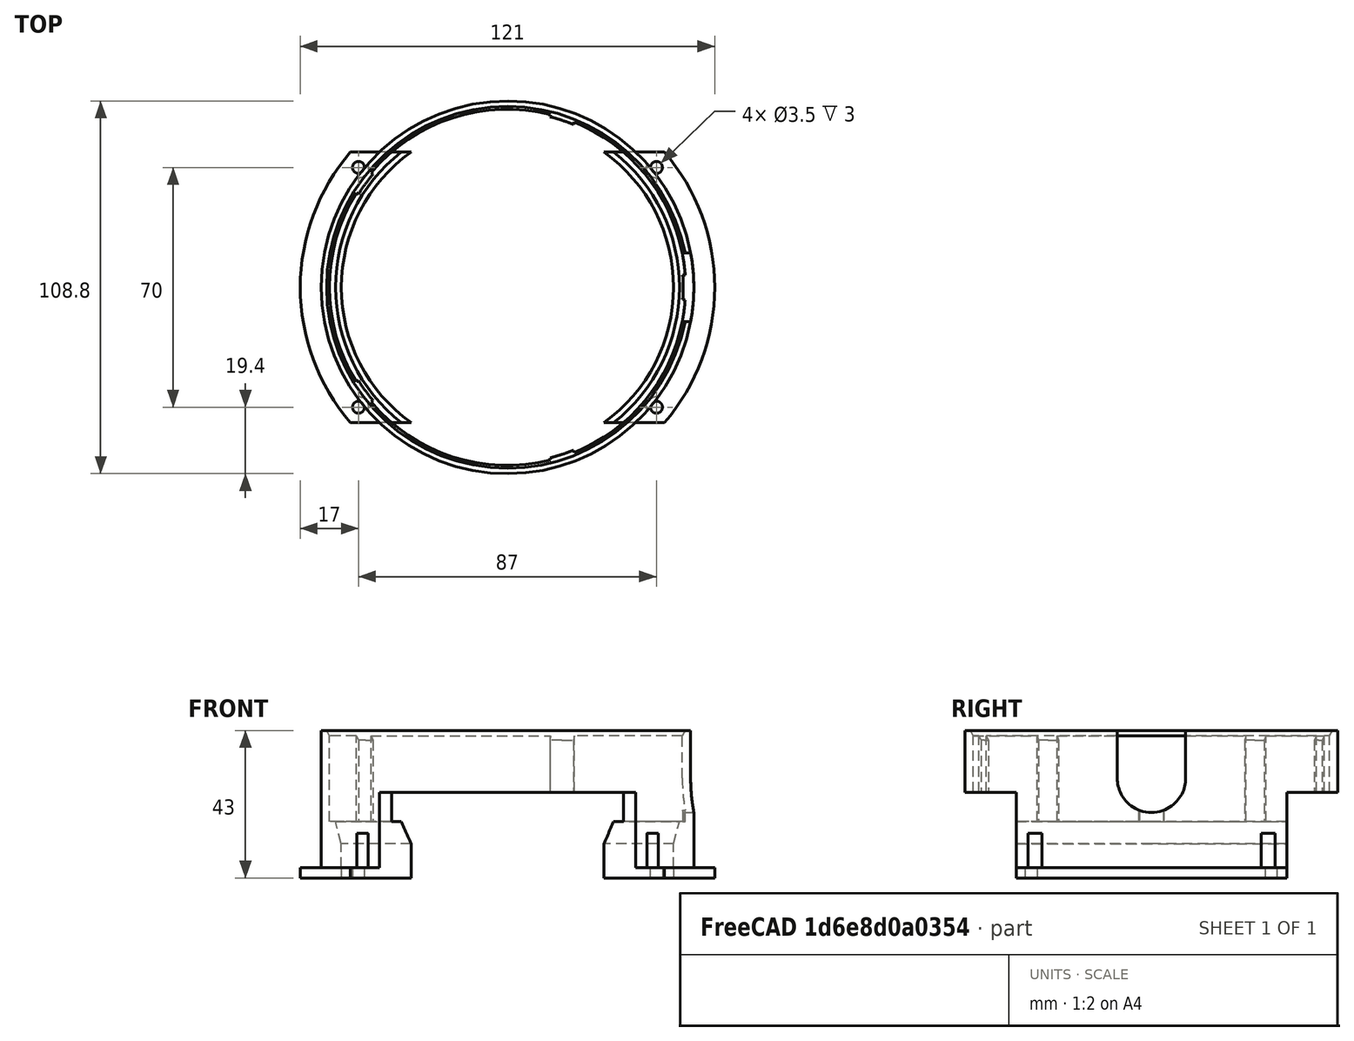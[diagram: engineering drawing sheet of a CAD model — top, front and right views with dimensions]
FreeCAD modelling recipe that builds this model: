
FCSTD DOCUMENT  (FreeCAD 0.19R24291 (Git))
Label: Фланец стаканов
License: All rights reserved
LicenseURL: http://en.wikipedia.org/wiki/All_rights_reserved
objects: Sketcher::SketchObject×6, PartDesign::Mirrored×4, PartDesign::Pocket×3, PartDesign::Revolution×2, PartDesign::MultiTransform×2, Mesh::Feature×1, PartDesign::Pad×1, PartDesign::PolarPattern×1, PartDesign::Plane×1, PartDesign::Body×1
note: 27 computed .brp shape members not serialized (recipe doc carries the construction recipe); baked Part::Feature solids carry a one-line shape summary decoded from their .brp

FEATURE [Mesh::Feature] ______________________________2  label="СъёмникСтаканов2"
FEATURE [Sketcher::SketchObject] Sketch
  FullyConstrained = true
  MapMode = 5
  Support = -> [XY_Plane]
  sketch-geometry (5):
    g0: ArcOfCircle CenterX=0 CenterY=0 CenterZ=0 NormalX=0 NormalY=0 NormalZ=1 AngleXU=0 Radius=60.5 StartAngle=0 EndAngle=1.5708
    g1: ArcOfCircle CenterX=0 CenterY=0 CenterZ=0 NormalX=0 NormalY=0 NormalZ=1 AngleXU=0 Radius=48.5 StartAngle=0 EndAngle=1.5708
    g2: LineSegment StartX=48.5 StartY=0 StartZ=0 EndX=60.5 EndY=0 EndZ=0
    g3: Circle CenterX=43.5 CenterY=35 CenterZ=0 NormalX=0 NormalY=0 NormalZ=1 AngleXU=0 Radius=1.75
    g4: LineSegment StartX=3.7e-15 StartY=60.5 StartZ=0 EndX=3e-15 EndY=48.5 EndZ=0
  constraints (15):
    c: Coincident(g0,g-1)
    c: PointOnObject(g0,g-1)
    c: Diameter(g0) = 121
    c: Coincident(g1,g0)
    c: PointOnObject(g1,g-1)
    c: Diameter(g1) = 97
    c: Coincident(g2,g1)
    c: Coincident(g2,g0)
    c: Diameter(g3) = 3.5
    c: DistanceX(g3) = 43.5
    c: DistanceY(g3) = 35
    c: PointOnObject(g1,g-2)
    c: PointOnObject(g0,g-2)
    c: Coincident(g4,g0)
    c: Coincident(g4,g1)
FEATURE [Sketcher::SketchObject] Sketch001
  FullyConstrained = true
  MapMode = 5
  Placement = pos=(0,0,0) rot=(1,0,0;1.5708rad)
  Support = -> [XZ_Plane]
  sketch-geometry (8):
    g0: LineSegment StartX=48.5 StartY=7 StartZ=0 EndX=50.2 EndY=13.5 EndZ=0
    g1: LineSegment StartX=50.2 StartY=13.5 StartZ=0 EndX=52 EndY=13.5 EndZ=0
    g2: LineSegment StartX=52 StartY=13.5 StartZ=0 EndX=52 EndY=38.5 EndZ=0
    g3: LineSegment StartX=52 StartY=38.5 StartZ=0 EndX=52.8 EndY=40 EndZ=0
    g4: LineSegment StartX=52.8 StartY=40 StartZ=0 EndX=54.4 EndY=40 EndZ=0
    g5: LineSegment StartX=54.4 StartY=40 StartZ=0 EndX=54.4 EndY=0 EndZ=0
    g6: LineSegment StartX=54.4 StartY=0 StartZ=0 EndX=48.5 EndY=0 EndZ=0
    g7: LineSegment StartX=48.5 StartY=0 StartZ=0 EndX=48.5 EndY=7 EndZ=0
  constraints (24):
    c: Coincident(g0,g1)
    c: Horizontal(g1)
    c: Coincident(g1,g2)
    c: Vertical(g2)
    c: Coincident(g2,g3)
    c: Coincident(g3,g4)
    c: Horizontal(g4)
    c: Coincident(g4,g5)
    c: Vertical(g5)
    c: Coincident(g5,g6)
    c: Horizontal(g6)
    c: Coincident(g6,g7)
    c: Coincident(g7,g0)
    c: Vertical(g7)
    c: Distance(g0,g-2) = 48.5
    c: Distance(g0,g-2) = 50.2
    c: Distance(g1,g-2) = 52
    c: Distance(g5) = 40
    c: Distance(g4) = 1.6
    c: Distance(g7) = 7
    c: Distance(g2) = 25
    c: DistanceY(g0,g0) = 6.5
    c: PointOnObject(g5,g-1)
    c: Distance(g1,g5) = 2.4
FEATURE [PartDesign::Revolution] Revolution
  Angle = 360
  Axis = (0,-2e-16,1)
  Base = (0,0,0)
  Placement = pos=(0,0,0) rot=(1,0,0;1.5708rad)
  Profile = -> Sketch001
  ReferenceAxis = -> Sketch001 [V_Axis]
  Reversed = true
FEATURE [PartDesign::Pad] Pad
  BaseFeature = -> Revolution
  Direction = (1,1,1)
  Length = 3
  Length2 = 100
  Placement = pos=(0,0,0) rot=(1,0,0;1.5708rad)
  Profile = -> Sketch
  Reversed = true
  Type = 0
FEATURE [Sketcher::SketchObject] Sketch002
  FullyConstrained = true
  MapMode = 5
  Support = -> [XY_Plane]
  sketch-geometry (1):
    g0: Circle CenterX=43.5 CenterY=35 CenterZ=0 NormalX=0 NormalY=0 NormalZ=1 AngleXU=0 Radius=3
  constraints (3):
    c: Diameter(g0) = 6
    c: DistanceX(g0) = 43.5
    c: DistanceY(g0) = 35
FEATURE [PartDesign::Pocket] Pocket
  BaseFeature = -> Pad
  Length = 10
  Length2 = 100
  Placement = pos=(0,0,0) rot=(1,0,0;1.5708rad)
  Profile = -> Sketch002
  Reversed = true
  Type = 0
FEATURE [Sketcher::SketchObject] Sketch003
  ExternalGeometry = -> [Pocket]
  FullyConstrained = true
  MapMode = 5
  Placement = pos=(0,0,0) rot=(1,0,0;1.5708rad)
  Support = -> [XZ_Plane]
  sketch-geometry (4):
    g0: LineSegment StartX=52 StartY=38.5 StartZ=0 EndX=51.3 EndY=37.1875 EndZ=0
    g1: LineSegment StartX=51.3 StartY=37.1875 StartZ=0 EndX=51.3 EndY=13.5 EndZ=0
    g2: LineSegment StartX=51.3 StartY=13.5 StartZ=0 EndX=52 EndY=13.5 EndZ=0
    g3: LineSegment StartX=52 StartY=13.5 StartZ=0 EndX=52 EndY=38.5 EndZ=0
  constraints (10):
    c: Coincident(g0,g1)
    c: Coincident(g1,g2)
    c: Coincident(g2,g3)
    c: Coincident(g3,g0)
    c: Horizontal(g2)
    c: Vertical(g1)
    c: DistanceX(g2,g2) = 0.7
    c: Coincident(g2,g-3)
    c: Coincident(g0,g-4)
    c: Parallel(g0,g-4)
FEATURE [PartDesign::Revolution] Revolution001
  Angle = 4
  Axis = (0,-2e-16,1)
  Base = (0,0,0)
  BaseFeature = -> Pocket
  Placement = pos=(0,0,0) rot=(1,0,0;1.5708rad)
  Profile = -> Sketch003
  ReferenceAxis = -> Sketch003 [V_Axis]
FEATURE [PartDesign::Mirrored] Mirrored
  MirrorPlane = -> Sketch [V_Axis]
  Placement = pos=(0,0,0) rot=(1,0,0;1.5708rad)
FEATURE [PartDesign::Mirrored] Mirrored001
  MirrorPlane = -> Sketch [H_Axis]
  Placement = pos=(0,0,0) rot=(1,0,0;1.5708rad)
FEATURE [PartDesign::MultiTransform] MultiTransform
  BaseFeature = -> Revolution001
  Originals = -> [Pad,Pocket]
  Placement = pos=(0,0,0) rot=(1,0,0;1.5708rad)
  Transformations = -> [Mirrored,Mirrored001]
FEATURE [PartDesign::Mirrored] Mirrored002
  MirrorPlane = -> XZ_Plane
  Placement = pos=(0,0,0) rot=(1,0,0;1.5708rad)
FEATURE [PartDesign::PolarPattern] PolarPattern
  Angle = 360
  Axis = -> Sketch003 [V_Axis]
  Occurrences = 5
  Placement = pos=(0,0,0) rot=(1,0,0;1.5708rad)
FEATURE [PartDesign::MultiTransform] MultiTransform001
  BaseFeature = -> MultiTransform
  Originals = -> [Revolution001]
  Placement = pos=(0,0,0) rot=(1,0,0;1.5708rad)
  Transformations = -> [Mirrored002,PolarPattern]
FEATURE [PartDesign::Plane] DatumPlane
  AttachmentOffset = pos=(0,0,0) rot=(0,1,0;1.5708rad)
  Length = 76.4018
  MapMode = 7
  Placement = pos=(54.4,-8.9e-15,40) rot=(0,1,0;1.5708rad)
  ResizeMode = 0
  Support = -> [MultiTransform001]
  Width = 61.4018
FEATURE [Sketcher::SketchObject] Sketch004
  FullyConstrained = false
  MapMode = 5
  Placement = pos=(54.4,-8.9e-15,40) rot=(0,1,0;1.5708rad)
  Support = -> [DatumPlane]
  sketch-geometry (5):
    g0: LineSegment StartX=0 StartY=0 StartZ=0 EndX=0 EndY=10 EndZ=0
    g1: LineSegment StartX=0 StartY=0 StartZ=0 EndX=0 EndY=-10 EndZ=0
    g2: LineSegment StartX=0 StartY=10 StartZ=0 EndX=13.8862 EndY=10 EndZ=0
    g3: LineSegment StartX=0 StartY=-10 StartZ=0 EndX=13.8862 EndY=-10 EndZ=0
    g4: ArcOfCircle CenterX=13.8862 CenterY=0 CenterZ=0 NormalX=0 NormalY=0 NormalZ=1 AngleXU=0 Radius=10 StartAngle=4.71239 EndAngle=7.85399
  constraints (14):
    c: Coincident(g0,g-1)
    c: PointOnObject(g0,g-2)
    c: Coincident(g1,g0)
    c: PointOnObject(g1,g-2)
    c: Coincident(g2,g0)
    c: Coincident(g3,g1)
    c: Horizontal(g3)
    c: PointOnObject(g4,g-1)
    c: Coincident(g4,g2)
    c: Coincident(g4,g3)
    c: Tangent(g3,g4)
    c: Tangent(g2,g4)
    c: Diameter(g4) = 20
    c: Horizontal(g2)
FEATURE [PartDesign::Pocket] Pocket001
  BaseFeature = -> MultiTransform001
  Length = 5
  Length2 = 100
  Placement = pos=(0,0,0) rot=(1,0,0;1.5708rad)
  Profile = -> Sketch004
  Type = 0
FEATURE [Sketcher::SketchObject] Sketch005
  FullyConstrained = false
  MapMode = 5
  Placement = pos=(0,0,0) rot=(0.57735,0.57735,0.57735;2.0944rad)
  Support = -> [YZ_Plane]
  sketch-geometry (4):
    g0: LineSegment StartX=39.5 StartY=-3 StartZ=0 EndX=61.2028 EndY=-3 EndZ=0
    g1: LineSegment StartX=61.2028 StartY=-3 StartZ=0 EndX=61.2028 EndY=22 EndZ=0
    g2: LineSegment StartX=61.2028 StartY=22 StartZ=0 EndX=39.5 EndY=22 EndZ=0
    g3: LineSegment StartX=39.5 StartY=22 StartZ=0 EndX=39.5 EndY=-3 EndZ=0
  constraints (11):
    c: Coincident(g0,g1)
    c: Coincident(g1,g2)
    c: Coincident(g2,g3)
    c: Coincident(g3,g0)
    c: Horizontal(g0)
    c: Horizontal(g2)
    c: Vertical(g1)
    c: Vertical(g3)
    c: Distance(g0,g-1) = 3
    c: Distance(g0,g-2) = 39.5
    c: Distance(g1) = 25
FEATURE [PartDesign::Pocket] Pocket002
  BaseFeature = -> Pocket001
  Length = 5
  Length2 = 100
  Midplane = true
  Placement = pos=(0,0,0) rot=(1,0,0;1.5708rad)
  Profile = -> Sketch005
  Type = 1
FEATURE [PartDesign::Mirrored] Mirrored003
  BaseFeature = -> Pocket002
  MirrorPlane = -> Sketch005 [V_Axis]
  Originals = -> [Pocket002]
  Placement = pos=(0,0,0) rot=(1,0,0;1.5708rad)
FEATURE [PartDesign::Body] Body
  Group = -> [Sketch,Sketch001,Revolution,Pad,Sketch002,Pocket,Sketch003,Revolution001,MultiTransform,Mirrored,Mirrored001,MultiTransform001,Mirrored002,PolarPattern,DatumPlane,Sketch004,Pocket001,Sketch005,Pocket002,Mirrored003]
  Origin = -> Origin
  Placement = pos=(0,0,3) rot=(0,0,1;0rad)
  Tip = -> Mirrored003
